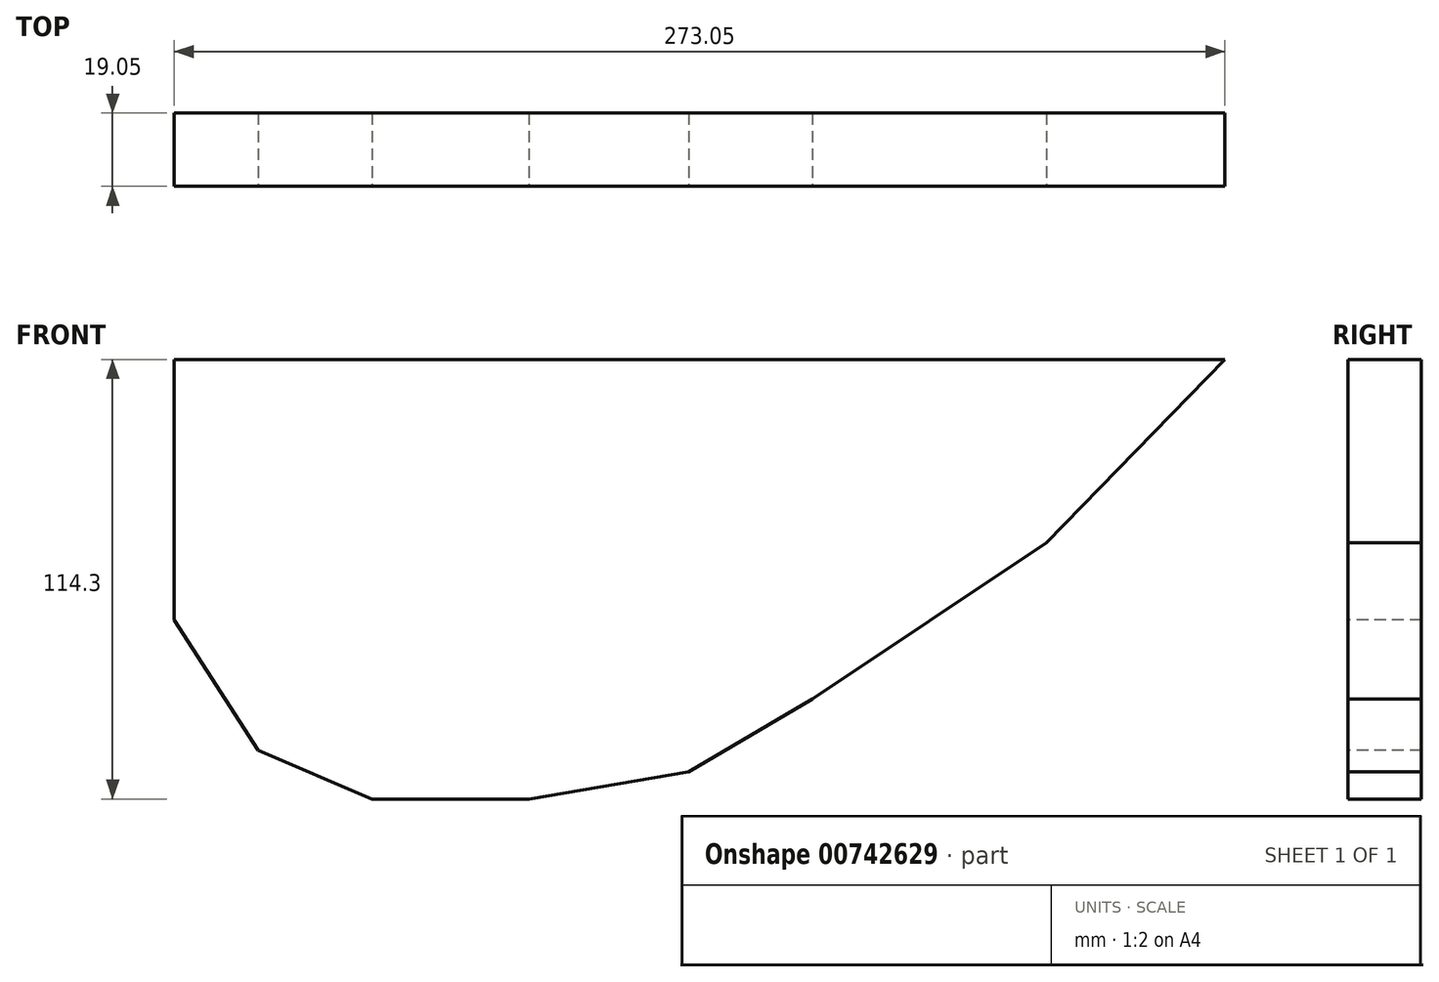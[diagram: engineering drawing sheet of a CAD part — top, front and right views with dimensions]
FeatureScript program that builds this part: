
annotation { "Feature Type Name" : "Feature", "Feature Type Description" : "" }
export const myFeature = defineFeature(function(context is Context, id is Id, definition is map)
    precondition{}
    {
        {
            var Q0;
            Q0=qCreatedBy(makeId("Front.planeOp"),FACE);
            var sketch = newSketch(context, id + "F0", { "sketchPlane" : qUnion([Q0])});
            skLineSegment(sketch, "E0.bottom", {"start": v(0, 0) * mm, "end": v(273.05, 0) * mm});
            skLineSegment(sketch, "E0.top", {"start": v(0, 114.3) * mm, "end": v(273.05, 114.3) * mm});
            skLineSegment(sketch, "E0.left", {"start": v(0, 0) * mm, "end": v(0, 114.3) * mm});
            skLineSegment(sketch, "E0.right", {"start": v(273.05, 0) * mm, "end": v(273.05, 114.3) * mm});
            skSolve(sketch);
        }
        {
            var Q0;
            Q0=makeQuery(id+"F0.imprint","IMPRINT",FACE,{"disambiguationData":[TD([[makeQuery(id+"F0.imprint","IMPRINT",EDGE,{"derivedFrom":sQuery(id+"F0.wireOp",EDGE,"E0.bottom")}),1.0]])]});
            extrude(context, id + "F1", {"entities" : qUnion([Q0]), "depth" : 19.05 * mm, "offsetDistance" : 25.4 * mm});
        }
        {
            var Q0;
            Q0=makeQuery(id+"F1.opExtrude","CAP_FACE",FACE,{"disambiguationData":[OSD([sQuery(id+"F0.wireOp",EDGE,"E0.bottom"),sQuery(id+"F0.wireOp",EDGE,"E0.top"),sQuery(id+"F0.wireOp",EDGE,"E0.left"),sQuery(id+"F0.wireOp",EDGE,"E0.right")])],"isStart":false});
            var sketch = newSketch(context, id + "F2", { "sketchPlane" : qUnion([Q0])});
            skLineSegment(sketch, "E1", {"start": v(0, 46.54) * mm, "end": v(21.85, 12.69) * mm});
            skLineSegment(sketch, "E2", {"start": v(21.85, 12.69) * mm, "end": v(51.42, 0) * mm});
            skLineSegment(sketch, "E3", {"start": v(51.42, 0) * mm, "end": v(92.12, 0) * mm});
            skLineSegment(sketch, "E4", {"start": v(92.12, 0) * mm, "end": v(133.68, 7.12) * mm});
            skLineSegment(sketch, "E5", {"start": v(133.68, 7.12) * mm, "end": v(165.82, 25.97) * mm});
            skLineSegment(sketch, "E6", {"start": v(165.82, 25.97) * mm, "end": v(226.66, 66.67) * mm});
            skLineSegment(sketch, "E7", {"start": v(226.66, 66.67) * mm, "end": v(273.05, 114.3) * mm});
            skLineSegment(sketch, "E8", {"start": v(273.05, 114.3) * mm, "end": v(273.05, 0) * mm});
            skLineSegment(sketch, "E9", {"start": v(273.05, 0) * mm, "end": v(0, 0) * mm});
            skLineSegment(sketch, "E10", {"start": v(0, 0) * mm, "end": v(0, 46.54) * mm});
            skSolve(sketch);
        }
        {
            var Q0;
            Q0=makeQuery(id+"F2.imprint","IMPRINT",FACE,{"disambiguationData":[TD([[makeQuery(id+"F2.imprint","IMPRINT",EDGE,{"derivedFrom":sQuery(id+"F2.wireOp",EDGE,"E1")}),-1.0]])]});
            var Q1;
            {var subQ0=sQuery(id+"F2.wireOp",EDGE,"E4");Q1=makeQuery(id+"F2.imprint","IMPRINT",FACE,{"disambiguationData":[TD([[makeQuery(id+"F2.imprint","IMPRINT",EDGE,{"derivedFrom":subQ0}),-1.0]])]});}
            extrude(context, id + "F3", {"entities" : qUnion([Q0, Q1]), "operationType" : NewBodyOperationType.REMOVE, "oppositeDirection" : true, "depth" : 25.4 * mm, "offsetDistance" : 25.4 * mm});
        }
    });
